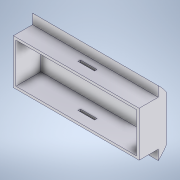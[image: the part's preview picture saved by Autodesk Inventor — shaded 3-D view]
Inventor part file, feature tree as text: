
AUTODESK INVENTOR PART (.ipt)
format: ipt  version: 2021 (Build 250183000, 183)  size: 219,136 bytes
history: native  units: mm
features: extrude x6, sketch x6, fillet x1
ambient origin geometry x8: Origin, YZ Plane, XZ Plane, XY Plane, X Axis, Y Axis, Z Axis, Center Point
bodies: Solid1 (feature_tree)
feature tree (13):
  extrude  "Extrusion1"  Depth=151.0mm
  extrude  "Extrusion2"  Depth=151.0mm
  extrude  "Extrusion3"  Depth=3.0mm
  fillet  "Fillet1"  Radius=3.0mm
  extrude  "Extrusion5"  Depth=3.0mm
  extrude  "Extrusion6"  Depth=30.0mm
  extrude  "Extrusion7"  Depth=10.0mm
  sketch  "Sketch1"  dims[d0=151.0mm d1=112.0mm]
  sketch  "Sketch2"  dims[d2=3.0mm d3=0.0mm d4=151.0mm]
  sketch  "Sketch3"  dims[d5=53.0mm d6=3.0mm d7=3.0mm]
  sketch  "Sketch6"  dims[d8=3.0mm d9=3.0mm]
  sketch  "Sketch7"  dims[d10=30.0mm d11=0.0mm d12=44.5mm]
  sketch  "Sketch8"  dims[d13=53.0mm d14=44.5mm d15=53.0mm d16=3.0mm d17=3.0mm d18=3.0mm d19=20.0mm d20=35.0mm d21=12.0mm d22=18.0mm d23=3.0mm d24=3.0mm d25=3.0mm d26=8.0mm d27=0.0mm d28=4.0mm d35=1.0mm d36=1.0mm d37=20.0mm d38=3.0mm d39=65.5mm d40=12.0mm d41=8.0mm d42=0.0mm d43=10.0mm d44=0.0mm d45=90.0deg d46=10.0mm d47=0.0mm]
